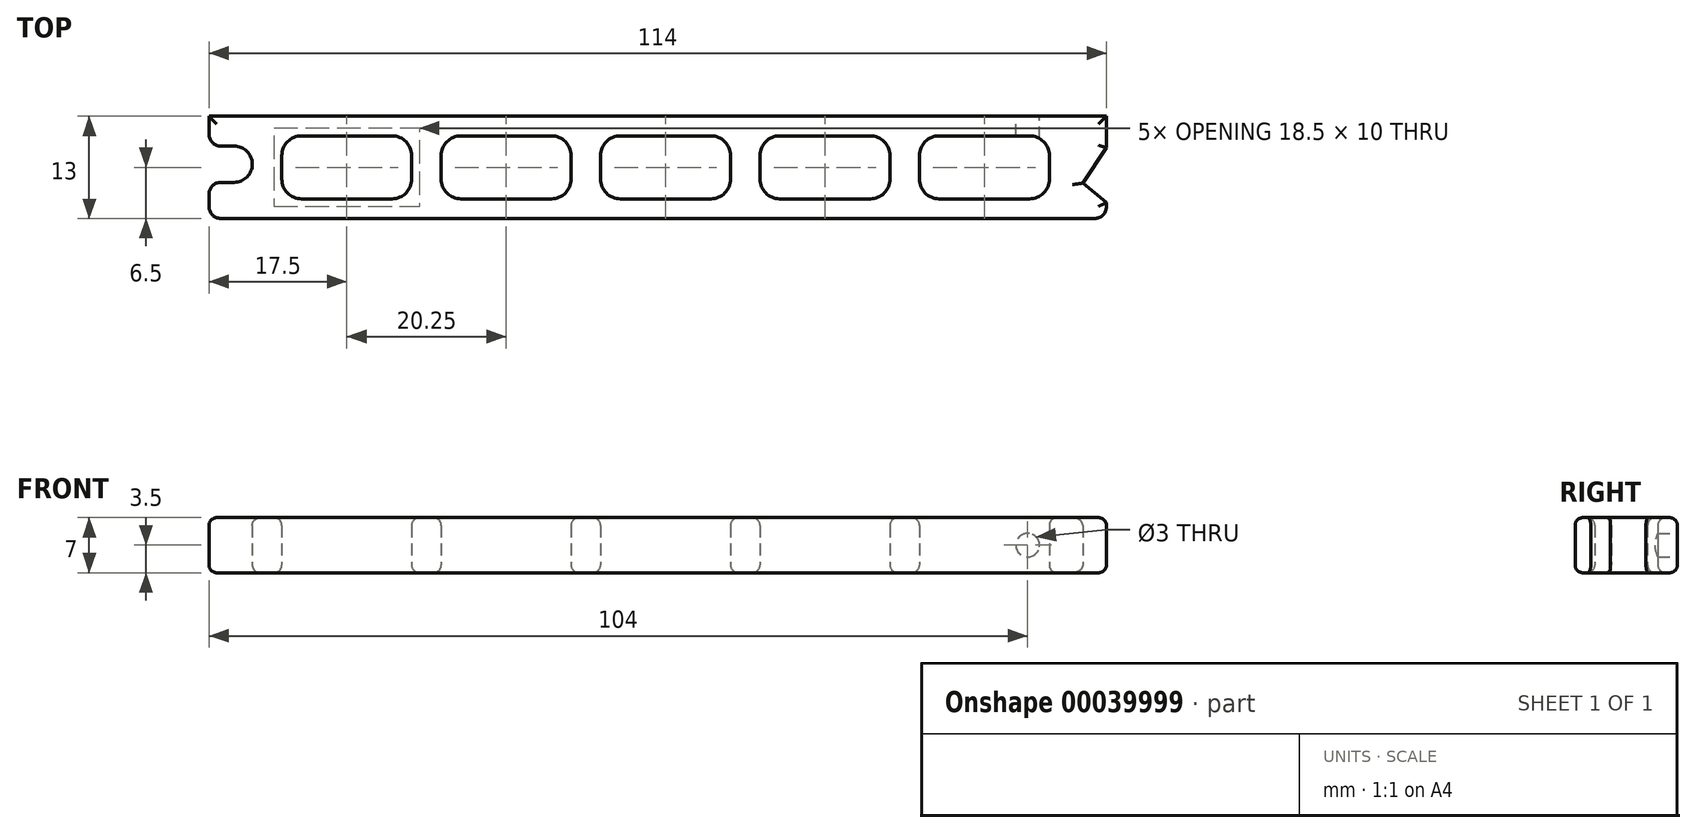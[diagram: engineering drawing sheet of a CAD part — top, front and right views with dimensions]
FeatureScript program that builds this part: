
annotation { "Feature Type Name" : "Feature", "Feature Type Description" : "" }
export const myFeature = defineFeature(function(context is Context, id is Id, definition is map)
    precondition{}
    {
        {
            var Q0;
            Q0=qCreatedBy(makeId("Top.planeOp"),FACE);
            var sketch = newSketch(context, id + "F0", { "sketchPlane" : qUnion([Q0])});
            skLineSegment(sketch, "E0.bottom", {"start": v(1.5, 0) * mm, "end": v(112.5, 0) * mm});
            skLineSegment(sketch, "E0.top", {"start": v(0, 13) * mm, "end": v(114, 13) * mm});
            skLineSegment(sketch, "E1", {"start": v(0, 13) * mm, "end": v(0, 10.7) * mm});
            skLineSegment(sketch, "E2.bottom", {"start": v(1.5, 4.6) * mm, "end": v(3.2, 4.6) * mm});
            skLineSegment(sketch, "E2.top", {"start": v(1.5, 9.2) * mm, "end": v(3.2, 9.2) * mm});
            skArc(sketch, "E3", {"start": v(3.2, 4.6) * mm, "mid": v(5.5, 6.9) * mm, "end": v(3.2, 9.2) * mm});
            skLineSegment(sketch, "E4.trimOffspring", {"start": v(0, 3.1) * mm, "end": v(0, 1.5) * mm});
            skLineSegment(sketch, "E5", {"start": v(0, 9.2) * mm, "end": v(0, 4.6) * mm, "construction": true});
            skLineSegment(sketch, "E6", {"start": v(0, 6.9) * mm, "end": v(3.2, 6.9) * mm, "construction": true});
            skLineSegment(sketch, "E7", {"start": v(114, 13) * mm, "end": v(114, 9) * mm});
            skLineSegment(sketch, "E8", {"start": v(114, 2) * mm, "end": v(114, 1.5) * mm});
            skPoint(sketch, "E9.visualSharp", {"position": v(114, 0) * mm});
            skArc(sketch, "E9.filletArc", {"start": v(112.5, 0) * mm, "mid": v(113.56, 0.44) * mm, "end": v(114, 1.5) * mm});
            skPoint(sketch, "E10.visualSharp", {"position": v(0, 0) * mm});
            skArc(sketch, "E10.filletArc", {"start": v(0, 1.5) * mm, "mid": v(0.44, 0.44) * mm, "end": v(1.5, 0) * mm});
            skPoint(sketch, "E11.visualSharp", {"position": v(0, 4.6) * mm});
            skArc(sketch, "E11.filletArc", {"start": v(1.5, 4.6) * mm, "mid": v(0.44, 4.16) * mm, "end": v(0, 3.1) * mm});
            skPoint(sketch, "E12.visualSharp", {"position": v(0, 9.2) * mm});
            skArc(sketch, "E12.filletArc", {"start": v(0, 10.7) * mm, "mid": v(0.44, 9.64) * mm, "end": v(1.5, 9.2) * mm});
            skPoint(sketch, "E13.visualSharp", {"position": v(114, 4.5) * mm});
            skLineSegment(sketch, "E14", {"start": v(114, 4.5) * mm, "end": v(111, 4.5) * mm, "construction": true});
            skLineSegment(sketch, "E15", {"start": v(114, 9) * mm, "end": v(111, 4.5) * mm});
            skLineSegment(sketch, "E16", {"start": v(114, 2) * mm, "end": v(111, 4.5) * mm});
            skSolve(sketch);
        }
        {
            var Q0;
            Q0=makeQuery(id+"F0.imprint","IMPRINT",FACE,{"disambiguationData":[TD([[makeQuery(id+"F0.imprint","IMPRINT",EDGE,{"derivedFrom":sQuery(id+"F0.wireOp",EDGE,"E0.bottom")}),1.0]])]});
            extrude(context, id + "F1", {"entities" : qUnion([Q0]), "depth" : 7 * mm});
        }
        {
            var Q0;
            Q0=makeQuery(id+"F1.opExtrude","CAP_FACE",FACE,{"disambiguationData":[OSD([sQuery(id+"F0.wireOp",EDGE,"E0.bottom"),sQuery(id+"F0.wireOp",EDGE,"E0.top"),sQuery(id+"F0.wireOp",EDGE,"E1"),sQuery(id+"F0.wireOp",EDGE,"E2.bottom"),sQuery(id+"F0.wireOp",EDGE,"E2.top"),sQuery(id+"F0.wireOp",EDGE,"E3"),sQuery(id+"F0.wireOp",EDGE,"E4.trimOffspring"),sQuery(id+"F0.wireOp",EDGE,"E7"),sQuery(id+"F0.wireOp",EDGE,"c30ca287-96d4-4dfe-8688-3bdeec023004"),sQuery(id+"F0.wireOp",EDGE,"f645941c-dc99-4dda-a8e2-c4b280260802"),sQuery(id+"F0.wireOp",EDGE,"E8")])],"isStart":true});
            var sketch = newSketch(context, id + "F2", { "sketchPlane" : qUnion([Q0])});
            skLineSegment(sketch, "E17.bottom", {"start": v(104.25, -2.5) * mm, "end": v(92.75, -2.5) * mm});
            skLineSegment(sketch, "E17.top", {"start": v(104.25, -10.5) * mm, "end": v(92.75, -10.5) * mm});
            skLineSegment(sketch, "E17.left", {"start": v(106.75, -5) * mm, "end": v(106.75, -8) * mm});
            skLineSegment(sketch, "E17.right", {"start": v(90.25, -5) * mm, "end": v(90.25, -8) * mm});
            skLineSegment(sketch, "E18", {"start": v(106.75, -10.5) * mm, "end": v(106.75, -13) * mm, "construction": true});
            skLineSegment(sketch, "E19", {"start": v(106.75, -2.5) * mm, "end": v(106.75, 0) * mm, "construction": true});
            skPoint(sketch, "E20.visualSharp", {"position": v(90.25, -10.5) * mm});
            skArc(sketch, "E20.filletArc", {"start": v(90.25, -8) * mm, "mid": v(90.98, -9.77) * mm, "end": v(92.75, -10.5) * mm});
            skPoint(sketch, "E21.visualSharp", {"position": v(90.25, -2.5) * mm});
            skArc(sketch, "E21.filletArc", {"start": v(92.75, -2.5) * mm, "mid": v(90.98, -3.23) * mm, "end": v(90.25, -5) * mm});
            skPoint(sketch, "E22.visualSharp", {"position": v(106.75, -2.5) * mm});
            skArc(sketch, "E22.filletArc", {"start": v(106.75, -5) * mm, "mid": v(106.02, -3.23) * mm, "end": v(104.25, -2.5) * mm});
            skPoint(sketch, "E23.visualSharp", {"position": v(106.75, -10.5) * mm});
            skArc(sketch, "E23.filletArc", {"start": v(104.25, -10.5) * mm, "mid": v(106.02, -9.77) * mm, "end": v(106.75, -8) * mm});
            skLineSegment(sketch, "E24.1.0.0", {"start": v(84, -2.5) * mm, "end": v(72.5, -2.5) * mm});
            skPoint(sketch, "E24.1.0.1", {"position": v(86.5, -2.5) * mm});
            skLineSegment(sketch, "E24.1.0.2", {"start": v(84, -10.5) * mm, "end": v(72.5, -10.5) * mm});
            skPoint(sketch, "E24.1.0.3", {"position": v(86.5, -10.5) * mm});
            skLineSegment(sketch, "E24.1.0.4", {"start": v(70, -5) * mm, "end": v(70, -8) * mm});
            skLineSegment(sketch, "E24.1.0.5", {"start": v(86.5, -5) * mm, "end": v(86.5, -8) * mm});
            skPoint(sketch, "E24.1.0.6", {"position": v(70, -2.5) * mm});
            skPoint(sketch, "E24.1.0.7", {"position": v(70, -10.5) * mm});
            skArc(sketch, "E24.1.0.8", {"start": v(72.5, -2.5) * mm, "mid": v(70.73, -3.23) * mm, "end": v(70, -5) * mm});
            skArc(sketch, "E24.1.0.9", {"start": v(70, -8) * mm, "mid": v(70.73, -9.77) * mm, "end": v(72.5, -10.5) * mm});
            skArc(sketch, "E24.1.0.10", {"start": v(86.5, -5) * mm, "mid": v(85.77, -3.23) * mm, "end": v(84, -2.5) * mm});
            skArc(sketch, "E24.1.0.11", {"start": v(84, -10.5) * mm, "mid": v(85.77, -9.77) * mm, "end": v(86.5, -8) * mm});
            skLineSegment(sketch, "E24.2.0.0", {"start": v(63.75, -2.5) * mm, "end": v(52.25, -2.5) * mm});
            skPoint(sketch, "E24.2.0.1", {"position": v(66.25, -2.5) * mm});
            skLineSegment(sketch, "E24.2.0.2", {"start": v(63.75, -10.5) * mm, "end": v(52.25, -10.5) * mm});
            skPoint(sketch, "E24.2.0.3", {"position": v(66.25, -10.5) * mm});
            skLineSegment(sketch, "E24.2.0.4", {"start": v(49.75, -5) * mm, "end": v(49.75, -8) * mm});
            skLineSegment(sketch, "E24.2.0.5", {"start": v(66.25, -5) * mm, "end": v(66.25, -8) * mm});
            skPoint(sketch, "E24.2.0.6", {"position": v(49.75, -2.5) * mm});
            skPoint(sketch, "E24.2.0.7", {"position": v(49.75, -10.5) * mm});
            skArc(sketch, "E24.2.0.8", {"start": v(52.25, -2.5) * mm, "mid": v(50.48, -3.23) * mm, "end": v(49.75, -5) * mm});
            skArc(sketch, "E24.2.0.9", {"start": v(49.75, -8) * mm, "mid": v(50.48, -9.77) * mm, "end": v(52.25, -10.5) * mm});
            skArc(sketch, "E24.2.0.10", {"start": v(66.25, -5) * mm, "mid": v(65.52, -3.23) * mm, "end": v(63.75, -2.5) * mm});
            skArc(sketch, "E24.2.0.11", {"start": v(63.75, -10.5) * mm, "mid": v(65.52, -9.77) * mm, "end": v(66.25, -8) * mm});
            skLineSegment(sketch, "E24.3.0.0", {"start": v(43.5, -2.5) * mm, "end": v(32, -2.5) * mm});
            skPoint(sketch, "E24.3.0.1", {"position": v(46, -2.5) * mm});
            skLineSegment(sketch, "E24.3.0.2", {"start": v(43.5, -10.5) * mm, "end": v(32, -10.5) * mm});
            skPoint(sketch, "E24.3.0.3", {"position": v(46, -10.5) * mm});
            skLineSegment(sketch, "E24.3.0.4", {"start": v(29.5, -5) * mm, "end": v(29.5, -8) * mm});
            skLineSegment(sketch, "E24.3.0.5", {"start": v(46, -5) * mm, "end": v(46, -8) * mm});
            skPoint(sketch, "E24.3.0.6", {"position": v(29.5, -2.5) * mm});
            skPoint(sketch, "E24.3.0.7", {"position": v(29.5, -10.5) * mm});
            skArc(sketch, "E24.3.0.8", {"start": v(32, -2.5) * mm, "mid": v(30.23, -3.23) * mm, "end": v(29.5, -5) * mm});
            skArc(sketch, "E24.3.0.9", {"start": v(29.5, -8) * mm, "mid": v(30.23, -9.77) * mm, "end": v(32, -10.5) * mm});
            skArc(sketch, "E24.3.0.10", {"start": v(46, -5) * mm, "mid": v(45.27, -3.23) * mm, "end": v(43.5, -2.5) * mm});
            skArc(sketch, "E24.3.0.11", {"start": v(43.5, -10.5) * mm, "mid": v(45.27, -9.77) * mm, "end": v(46, -8) * mm});
            skLineSegment(sketch, "E24.4.0.0", {"start": v(23.25, -2.5) * mm, "end": v(11.75, -2.5) * mm});
            skPoint(sketch, "E24.4.0.1", {"position": v(25.75, -2.5) * mm});
            skLineSegment(sketch, "E24.4.0.2", {"start": v(23.25, -10.5) * mm, "end": v(11.75, -10.5) * mm});
            skPoint(sketch, "E24.4.0.3", {"position": v(25.75, -10.5) * mm});
            skLineSegment(sketch, "E24.4.0.4", {"start": v(9.25, -5) * mm, "end": v(9.25, -8) * mm});
            skLineSegment(sketch, "E24.4.0.5", {"start": v(25.75, -5) * mm, "end": v(25.75, -8) * mm});
            skPoint(sketch, "E24.4.0.6", {"position": v(9.25, -2.5) * mm});
            skPoint(sketch, "E24.4.0.7", {"position": v(9.25, -10.5) * mm});
            skArc(sketch, "E24.4.0.8", {"start": v(11.75, -2.5) * mm, "mid": v(9.98, -3.23) * mm, "end": v(9.25, -5) * mm});
            skArc(sketch, "E24.4.0.9", {"start": v(9.25, -8) * mm, "mid": v(9.98, -9.77) * mm, "end": v(11.75, -10.5) * mm});
            skArc(sketch, "E24.4.0.10", {"start": v(25.75, -5) * mm, "mid": v(25.02, -3.23) * mm, "end": v(23.25, -2.5) * mm});
            skArc(sketch, "E24.4.0.11", {"start": v(23.25, -10.5) * mm, "mid": v(25.02, -9.77) * mm, "end": v(25.75, -8) * mm});
            skLineSegment(sketch, "E24.direction1", {"start": v(92.75, -2.5) * mm, "end": v(72.5, -2.5) * mm, "construction": true});
            skSolve(sketch);
        }
        {
            var Q0;
            Q0=qSketchRegion(id+"F2",true);
            extrude(context, id + "F3", {"entities" : qUnion([Q0]), "operationType" : NewBodyOperationType.REMOVE, "endBound" : BoundingType.THROUGH_ALL, "oppositeDirection" : true, "depth" : 13.73 * mm});
        }
        {
            var Q0;
            Q0=makeQuery(id+"F1.opExtrude","CAP_FACE",FACE,{"disambiguationData":[OSD([sQuery(id+"F0.wireOp",EDGE,"E0.bottom"),sQuery(id+"F0.wireOp",EDGE,"E0.top"),sQuery(id+"F0.wireOp",EDGE,"E1"),sQuery(id+"F0.wireOp",EDGE,"E2.bottom"),sQuery(id+"F0.wireOp",EDGE,"E2.top"),sQuery(id+"F0.wireOp",EDGE,"E3"),sQuery(id+"F0.wireOp",EDGE,"E4.trimOffspring"),sQuery(id+"F0.wireOp",EDGE,"E7"),sQuery(id+"F0.wireOp",EDGE,"E8"),sQuery(id+"F0.wireOp",EDGE,"E9.filletArc"),sQuery(id+"F0.wireOp",EDGE,"E10.filletArc"),sQuery(id+"F0.wireOp",EDGE,"E11.filletArc"),sQuery(id+"F0.wireOp",EDGE,"E12.filletArc"),sQuery(id+"F0.wireOp",EDGE,"E15"),sQuery(id+"F0.wireOp",EDGE,"E16")])],"isStart":true});
            var Q1;
            Q1=makeQuery(id+"F1.opExtrude","CAP_FACE",FACE,{"disambiguationData":[OSD([sQuery(id+"F0.wireOp",EDGE,"E0.bottom"),sQuery(id+"F0.wireOp",EDGE,"E0.top"),sQuery(id+"F0.wireOp",EDGE,"E1"),sQuery(id+"F0.wireOp",EDGE,"E2.bottom"),sQuery(id+"F0.wireOp",EDGE,"E2.top"),sQuery(id+"F0.wireOp",EDGE,"E3"),sQuery(id+"F0.wireOp",EDGE,"E4.trimOffspring"),sQuery(id+"F0.wireOp",EDGE,"E7"),sQuery(id+"F0.wireOp",EDGE,"E8"),sQuery(id+"F0.wireOp",EDGE,"E9.filletArc"),sQuery(id+"F0.wireOp",EDGE,"E10.filletArc"),sQuery(id+"F0.wireOp",EDGE,"E11.filletArc"),sQuery(id+"F0.wireOp",EDGE,"E12.filletArc"),sQuery(id+"F0.wireOp",EDGE,"E15"),sQuery(id+"F0.wireOp",EDGE,"E16")])],"isStart":false});
            fillet(context, id + "F4", {"entities" : qUnion([Q0, Q1]), "radius" : 1 * mm, "allowEdgeOverflow" : false});
        }
        {
            var Q0;
            Q0=makeQuery(id+"F1.opExtrude","SWEPT_FACE",FACE,{"disambiguationData":[OSD([sQuery(id+"F0.wireOp",EDGE,"E0.top")])]});
            var sketch = newSketch(context, id + "F5", { "sketchPlane" : qUnion([Q0])});
            skLineSegment(sketch, "E25", {"start": v(-104, 1) * mm, "end": v(-104, 6) * mm, "construction": true});
            skCircle(sketch, "E26", {"center": v(-104, 3.5) * mm, "radius": 1.5 * mm});
            skSolve(sketch);
        }
        {
            var Q0;
            Q0=makeQuery(id+"F5.imprint","IMPRINT",FACE,{"disambiguationData":[TD([[makeQuery(id+"F5.imprint","IMPRINT",EDGE,{"derivedFrom":sQuery(id+"F5.wireOp",EDGE,"E26")}),1.0]])]});
            extrude(context, id + "F6", {"entities" : qUnion([Q0]), "operationType" : NewBodyOperationType.REMOVE, "endBound" : BoundingType.UP_TO_NEXT, "oppositeDirection" : true, "depth" : 25 * mm});
        }
    });
